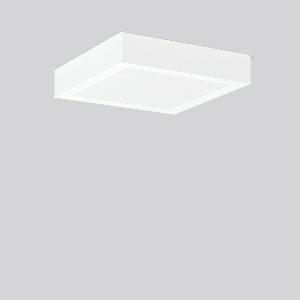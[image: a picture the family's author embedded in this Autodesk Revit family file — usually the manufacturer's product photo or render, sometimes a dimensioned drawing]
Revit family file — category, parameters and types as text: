
# Revit family: toledo_flat_square_a_672278_002_04_0026
name_source: partatom
category: Lighting Fixtures
units: mm (PartAtom-declared; Revit-internal decimal feet)

## family parameters
Cut with Voids When Loaded = No
Host = Face
Light Source = No
Part Type = Normal
Room Calculation Point = No
Round Connector Dimension = Use Diameter
Shared = No

## types (1)
- TOLEDO FLAT square A (1 x LED Modul 830, 2050 lm, 3000)
    Apparent Load = 25 VA
    CIE Flux Codes = 48 80 96 100 100
    Color Rendering = 80
    Color Temperature = 3000
    Default Elevation = 1800 mm
    Description = Series: TOLEDO FLAT square
Ultra thin surface mounted downlight. For escape route illumination. Surface mounted housing: sheet steel, powder-coated. Square cover plate: die-cast aluminium, powder coated. Light guide and diffuser made of non-yellowing PMMA, opal matt. Self-contained system with automatic self-test and feedback to the RZB monitoring system MULTIDIGIT. 
Colour: white
Length: 300 mm
Width: 300 mm
Height: 58 mm
Weight: 3.96 kg
Operating mode: maintained power mode
Duration time: 8 h
Lamp: LED
Socket: without socket
Colour temperature: 3000K
Colour rendering index (CRI): 80
System power: 25 W
Rated luminous flux: 2050 lm
Luminous flux, emergency: 170 lm
System power, emergency: -
Control gear: Regulated power supply
Protection class: I
Type of protection: IP 40
    Height = 58 mm
    Lamp = 1 x LED Modul 830
    Lamp Light Flux = 2050 lm
    Lamp count = 1
    Length = 300 mm
    Lifetime = 50000 h
    Luminous efficacy = 82 lm/W
    Manufacturer = RZB
    ModVariant = No
    Model = 672278.002.04
    Mounting Place = Ceiling
    Mounting Type = Surface mounted
    Number of Poles = 1
    OnlyDefault = Yes
    Power Factor = 1
    Product Name = TOLEDO FLAT square A
    Product group = Surface mounted downlights
    ProductGroupID = 302
    Protection Class = Protection class I
    Protection Degree = IP 40
    RLX_Detail_Level = 1
    RLX_Emergency_Light_Flux = 170 lm
    RLX_Emergency_Type = 3
    RLX_Emergency_Type_DB = Yes
    RlxData = <blob elided: 14017 chars, md5=60417baf>
    Socket = socket
    Standby Power = 0 W
    System Light Flux = 2050 lm
    System Power = 25 W
    Type Comments = Product without accessories
    Type Image = 901554.002.jpg
    URL = http://relux.com
    VarID = ---
    Voltage = 0 V
    Weight = 0.00 kg
    Width = 300 mm

## geometry (parser evidence)
native form markers: Sweep x11
no freeform markers — native parametric forms only
